# Revit family: 1419xxx Astro Incline Single
name_source: partatom
category: Lighting Fixtures
units: mm (PartAtom-declared; Revit-internal decimal feet)

## family parameters
Always vertical = Yes
Cut with Voids When Loaded = No
Host = Wall
Light Source = Yes
OmniClass Number = 23.80.70.00
OmniClass Title = Lighting
Part Type = Normal
Room Calculation Point = No
Round Connector Dimension = Use Diameter
Shared = No

## types (1)
- Astro Incline Single
    ADA compliant = N / A
    Color Filter = 16777215
    Default Elevation = 0 mm  [stored 0 ft]
    Dimmable = NO
    Dimming Lamp Color Temperature Shift = <None>
    Driver Included = Yes
    Efficacy (lm/w) = 59
    Electrical Class = 1
    Emit from Line Length = 610 mm
    Lamp = LED
    Light Source Fixed = Yes
    Location / IP Rating = IP65
    Main Finish = Antique Brass
    Main Material = Metal - Brass
    Manufacturer = Astro Lighting Ltd
    Manufacturer URL - Europe and Rest of World = www.astrolighting.com
    Manufacturer URL - North America = us.astrolighting.com
    Photometric Web File = 1419002_Incline Single Coastal Brass_Photometry_IES_Iss. 01.ies
    Power (Watts) = 8.2
    Product CCT = 3000K
    Product CRI = 80
    Product Dimensions (MM) = 220 x 122 x 58
    Product Location = Outdoor
    Product Name = Incline Single
    Product SKU = 1419002
    Product URL = https://www.astrolighting.com
    Product Weight (KG) = 1.81
    Tilt Angle = 60.00°
    URL = www.astrolighting.com

note: [stored X ft] marks values corroborated as IEEE doubles in the binary element streams (Revit-internal decimal feet)

## geometry (parser evidence)
native form markers: Sweep x1
no freeform markers — native parametric forms only
